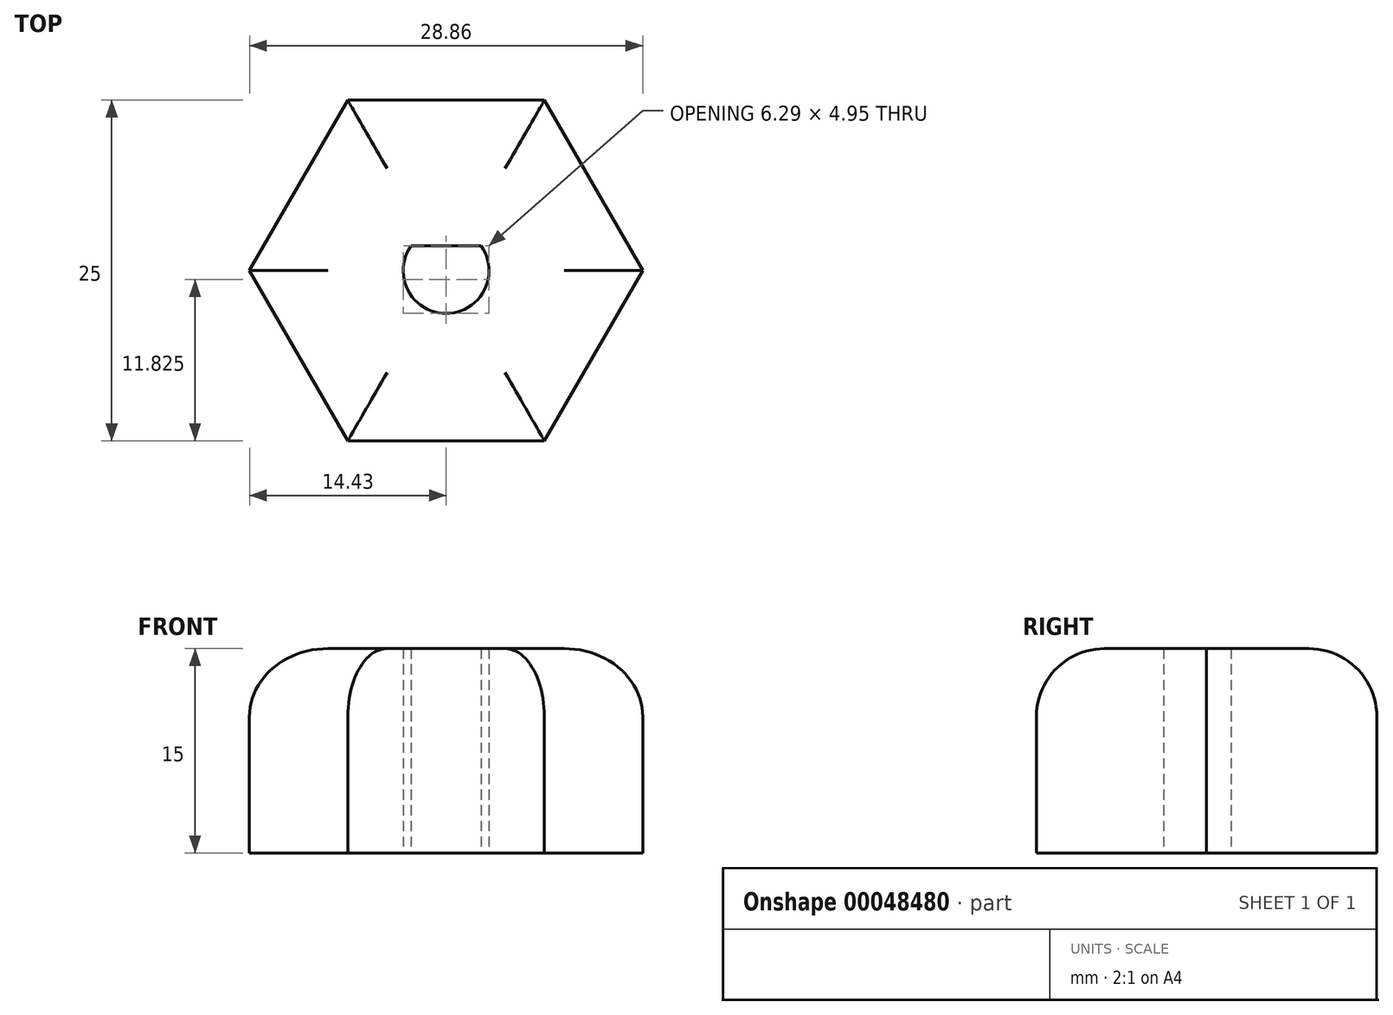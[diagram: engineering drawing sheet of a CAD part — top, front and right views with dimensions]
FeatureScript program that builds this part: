
annotation { "Feature Type Name" : "Feature", "Feature Type Description" : "" }
export const myFeature = defineFeature(function(context is Context, id is Id, definition is map)
    precondition{}
    {
        {
            var Q0;
            Q0=qCreatedBy(makeId("Top.planeOp"),FACE);
            var sketch = newSketch(context, id + "F0", { "sketchPlane" : qUnion([Q0])});
            skArc(sketch, "E0", {"start": v(-2.59, 1.8) * mm, "mid": v(0, -3.15) * mm, "end": v(2.59, 1.8) * mm});
            skLineSegment(sketch, "E1", {"start": v(-2.59, 1.8) * mm, "end": v(2.59, 1.8) * mm});
            skCircle(sketch, "E2.cCircle", {"center": v(0, 0) * mm, "radius": 12.5 * mm, "construction": true});
            skLineSegment(sketch, "E2.0", {"start": v(7.22, 12.5) * mm, "end": v(14.43, 0) * mm});
            skLineSegment(sketch, "E2.1", {"start": v(14.43, 0) * mm, "end": v(7.22, -12.5) * mm});
            skLineSegment(sketch, "E2.2", {"start": v(7.22, -12.5) * mm, "end": v(-7.22, -12.5) * mm});
            skLineSegment(sketch, "E2.3", {"start": v(-7.22, -12.5) * mm, "end": v(-14.43, 0) * mm});
            skLineSegment(sketch, "E2.4", {"start": v(-14.43, 0) * mm, "end": v(-7.22, 12.5) * mm});
            skLineSegment(sketch, "E2.5", {"start": v(-7.22, 12.5) * mm, "end": v(7.22, 12.5) * mm});
            skPoint(sketch, "E2.0.midPoint", {"position": v(10.83, 6.25) * mm});
            skSolve(sketch);
        }
        {
            var Q0;
            Q0=makeQuery(id+"F0.imprint","IMPRINT",FACE,{"disambiguationData":[TD([[makeQuery(id+"F0.imprint","IMPRINT",EDGE,{"derivedFrom":sQuery(id+"F0.wireOp",EDGE,"E0")}),-1.0]])]});
            extrude(context, id + "F1", {"entities" : qUnion([Q0]), "depth" : 15 * mm});
        }
        {
            var Q0;
            Q0=makeQuery(id+"F1.opExtrude","CAP_EDGE",EDGE,{"disambiguationData":[OSD([sQuery(id+"F0.wireOp",EDGE,"E2.2")])],"isStart":false});
            var Q1;
            Q1=makeQuery(id+"F1.opExtrude","CAP_EDGE",EDGE,{"disambiguationData":[OSD([sQuery(id+"F0.wireOp",EDGE,"E2.1")])],"isStart":false});
            var Q2;
            Q2=makeQuery(id+"F1.opExtrude","CAP_EDGE",EDGE,{"disambiguationData":[OSD([sQuery(id+"F0.wireOp",EDGE,"E2.0")])],"isStart":false});
            var Q3;
            Q3=makeQuery(id+"F1.opExtrude","CAP_EDGE",EDGE,{"disambiguationData":[OSD([sQuery(id+"F0.wireOp",EDGE,"E2.5")])],"isStart":false});
            var Q4;
            Q4=makeQuery(id+"F1.opExtrude","CAP_EDGE",EDGE,{"disambiguationData":[OSD([sQuery(id+"F0.wireOp",EDGE,"E2.4")])],"isStart":false});
            var Q5;
            Q5=makeQuery(id+"F1.opExtrude","CAP_EDGE",EDGE,{"disambiguationData":[OSD([sQuery(id+"F0.wireOp",EDGE,"E2.3")])],"isStart":false});
            fillet(context, id + "F2", {"entities" : qUnion([Q0, Q1, Q2, Q3, Q4, Q5]), "radius" : 5 * mm, "tangentPropagation" : true, "allowEdgeOverflow" : false});
        }
    });
